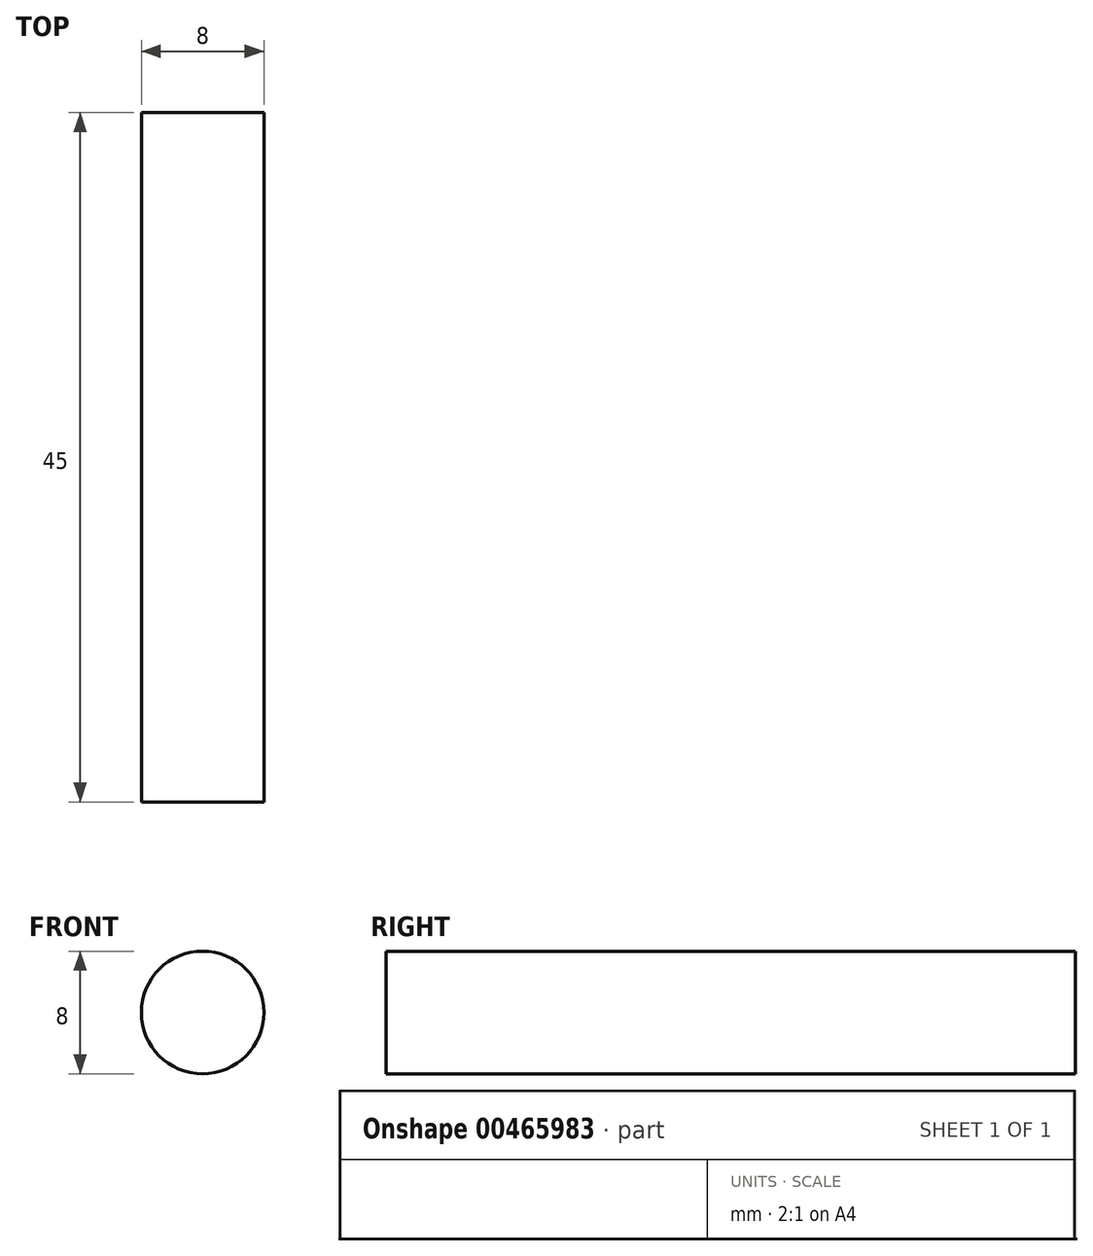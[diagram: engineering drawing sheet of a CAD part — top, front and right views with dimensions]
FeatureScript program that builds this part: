
annotation { "Feature Type Name" : "Feature", "Feature Type Description" : "" }
export const myFeature = defineFeature(function(context is Context, id is Id, definition is map)
    precondition{}
    {
        {
            var Q0;
            Q0=qCreatedBy(makeId("Right.planeOp"),FACE);
            var sketch = newSketch(context, id + "F0", { "sketchPlane" : qUnion([Q0])});
            skLineSegment(sketch, "E0.bottom", {"start": v(22.5, 0) * mm, "end": v(-22.5, 0) * mm});
            skLineSegment(sketch, "E0.top", {"start": v(22.5, 4) * mm, "end": v(-22.5, 4) * mm});
            skLineSegment(sketch, "E0.left", {"start": v(22.5, 0) * mm, "end": v(22.5, 4) * mm});
            skLineSegment(sketch, "E0.right", {"start": v(-22.5, 0) * mm, "end": v(-22.5, 4) * mm});
            skPoint(sketch, "E0.middle", {"position": v(0, 2) * mm});
            skSolve(sketch);
        }
        {
            var Q0;
            Q0=makeQuery(id+"F0.imprint","IMPRINT",FACE,{"disambiguationData":[TD([[makeQuery(id+"F0.imprint","IMPRINT",EDGE,{"derivedFrom":sQuery(id+"F0.wireOp",EDGE,"E0.bottom")}),-1.0]])]});
            var Q1;
            Q1=sQuery(id+"F0.wireOp",EDGE,"E0.bottom");
            revolve(context, id + "F1", {"entities" : qUnion([Q0]), "axis" : qUnion([Q1]), "revolveType" : RevolveType.FULL});
        }
    });
